# Revit family: FaEl_ExteriorInd
name_source: partatom
category: Fassadenelemente
units: mm (PartAtom-declared; Revit-internal decimal feet)

## family parameters
Beim Laden mit Abzugskörper schneiden = Nein
Gemeinsam genutzt = Nein
Immer vertikal = Ja
OmniClass-Nummer = 23.25.00.00
OmniClass-Titel = Structural and Space Division Products

## types (3) — shared parameters
Analytische Konstruktion = <Keine Auswahl>
Apparent_Density = 1.35 g/cm³
AssetType = Fixed
Certification = CE- marked, BBA 12/4937
Combustible = Nein
Core = Brown core, F-quality
Duration_Unit = year
Features = Graffitti-resistant, weather-resistant, flame-retardant core, lightfast, double-hardened, scratch and solvent resistant, easy to clean, custom shapes also available
Finish_Options = Slabs, triangle, cone, bowl, wave small grey, wave gold large, naturell, letter, bubble, knitter
FireRating = Euroclass B-s2, d0
Flexural_Strength = ≥ 90 MPa
Grade = To BS EN 438-6, Type EDF
IfcExportAs = IfcCoveringType
IfcExportType = NOTDEFINED
IsExternal = Ja
Manufacturer_Name = FunderMax GmbH
Manufacturer_URL = http://www.fundermax.at
Modulus_Of-Elasticity = ≥ 9.0 MPa
Panel_Material = FunderMax_CompactExterior
Panel_Thickness = 10 mm  [stored 0.0328084 ft]
Product_Information = www.ribaproductselector.com/Docs/0/27580/external/COL394192.pdf
Shape = Rectangle
Surface = NT
Tensile_Strength = ≥ 80 MPa
Thermal_Conductivity = 0.3 W/mK
Thermal_Expansion_Coefficient = 18x10^-6 1/K
Thickness_Options = 2-15 mm
Tolerances = 0-10 mm to BS EN 438-6
Version = 3
Warranty_Duration_Unit = year
Water_Vapour_Diffusion_Resistance = 17.200 μ

## per-type parameters (varying)
| type | Panel_Size_Length | Panel_Size_Width | Size |
| 4100x1300x0010_F_Quality | 4100 | 1300 | 4100x1300x10mm |
| 2800x1300x0010_F_Quality | 2800 | 1300 | 2800x1300x10mm |
| 2140x2060x0010_F_Quality | 2140 | 1060 | 2140x1060x10mm |

note: [stored X ft] marks values corroborated as IEEE doubles in the binary element streams (Revit-internal decimal feet)
